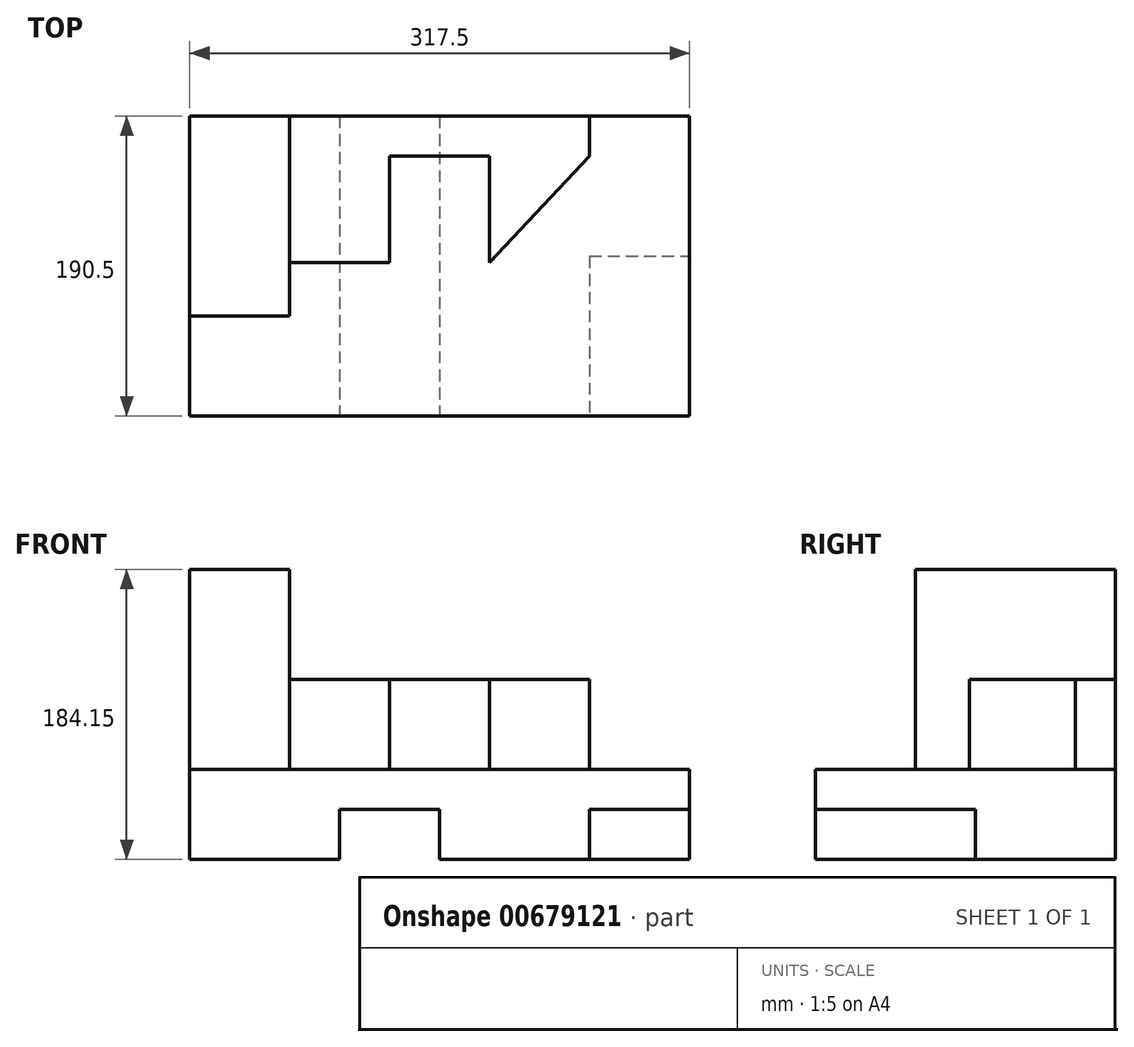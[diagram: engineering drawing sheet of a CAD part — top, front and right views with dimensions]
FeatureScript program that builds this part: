
annotation { "Feature Type Name" : "Feature", "Feature Type Description" : "" }
export const myFeature = defineFeature(function(context is Context, id is Id, definition is map)
    precondition{}
    {
        {
            var Q0;
            Q0=qCreatedBy(makeId("Front.planeOp"),FACE);
            var sketch = newSketch(context, id + "F0", { "sketchPlane" : qUnion([Q0])});
            skLineSegment(sketch, "E0.bottom", {"start": v(-158.75, 57.15) * mm, "end": v(158.75, 57.15) * mm});
            skLineSegment(sketch, "E0.top", {"start": v(-158.75, 0) * mm, "end": v(158.75, 0) * mm});
            skLineSegment(sketch, "E0.left", {"start": v(-158.75, 57.15) * mm, "end": v(-158.75, 0) * mm});
            skLineSegment(sketch, "E0.right", {"start": v(158.75, 57.15) * mm, "end": v(158.75, 0) * mm});
            skSolve(sketch);
        }
        {
            var Q0;
            Q0=makeQuery(id+"F0.imprint","IMPRINT",FACE,{"disambiguationData":[TD([[makeQuery(id+"F0.imprint","IMPRINT",EDGE,{"derivedFrom":sQuery(id+"F0.wireOp",EDGE,"E0.bottom")}),-1.0]])]});
            extrude(context, id + "F1", {"entities" : qUnion([Q0]), "oppositeDirection" : true, "depth" : 190.5 * mm, "offsetDistance" : 25.4 * mm});
        }
        {
            var Q0;
            Q0=makeQuery(id+"F1.opExtrude","CAP_FACE",FACE,{"disambiguationData":[OSD([sQuery(id+"F0.wireOp",EDGE,"E0.bottom"),sQuery(id+"F0.wireOp",EDGE,"E0.top"),sQuery(id+"F0.wireOp",EDGE,"E0.left"),sQuery(id+"F0.wireOp",EDGE,"E0.right")])],"isStart":true});
            var sketch = newSketch(context, id + "F2", { "sketchPlane" : qUnion([Q0])});
            skLineSegment(sketch, "E1", {"start": v(-63.5, 0) * mm, "end": v(-63.5, 31.75) * mm});
            skLineSegment(sketch, "E2", {"start": v(-63.5, 31.75) * mm, "end": v(0, 31.75) * mm});
            skLineSegment(sketch, "E3", {"start": v(0, 31.75) * mm, "end": v(0, 0) * mm});
            skLineSegment(sketch, "E4", {"start": v(0, 0) * mm, "end": v(-63.5, 0) * mm});
            skSolve(sketch);
        }
        {
            var Q0;
            Q0=makeQuery(id+"F2.imprint","IMPRINT",FACE,{"disambiguationData":[TD([[makeQuery(id+"F2.imprint","IMPRINT",EDGE,{"derivedFrom":sQuery(id+"F2.wireOp",EDGE,"E1")}),-1.0]])]});
            extrude(context, id + "F3", {"entities" : qUnion([Q0]), "operationType" : NewBodyOperationType.REMOVE, "endBound" : BoundingType.THROUGH_ALL, "oppositeDirection" : true, "depth" : 274.32 * mm, "offsetDistance" : 25.4 * mm});
        }
        {
            var Q0;
            Q0=makeQuery(id+"F0.imprint","IMPRINT",FACE,{"disambiguationData":[TD([[makeQuery(id+"F0.imprint","IMPRINT",EDGE,{"derivedFrom":sQuery(id+"F0.wireOp",EDGE,"E0.bottom")}),-1.0]])]});
            var sketch = newSketch(context, id + "F4", { "sketchPlane" : qUnion([Q0])});
            skLineSegment(sketch, "E5", {"start": v(158.75, 0) * mm, "end": v(158.75, 31.75) * mm});
            skLineSegment(sketch, "E6", {"start": v(158.75, 31.75) * mm, "end": v(95.25, 31.75) * mm});
            skLineSegment(sketch, "E7", {"start": v(95.25, 31.75) * mm, "end": v(95.25, 0) * mm});
            skLineSegment(sketch, "E8", {"start": v(95.25, 0) * mm, "end": v(158.75, 0) * mm});
            skSolve(sketch);
        }
        {
            var Q0;
            Q0=makeQuery(id+"F4.imprint","IMPRINT",FACE,{"disambiguationData":[TD([[makeQuery(id+"F4.imprint","IMPRINT",EDGE,{"derivedFrom":sQuery(id+"F4.wireOp",EDGE,"E5")}),-1.0]])]});
            extrude(context, id + "F5", {"entities" : qUnion([Q0]), "operationType" : NewBodyOperationType.REMOVE, "oppositeDirection" : true, "depth" : 101.6 * mm, "offsetDistance" : 25.4 * mm});
        }
        {
            var Q0;
            Q0=makeQuery(id+"F1.opExtrude","SWEPT_FACE",FACE,{"disambiguationData":[OSD([sQuery(id+"F0.wireOp",EDGE,"E0.bottom")])]});
            var sketch = newSketch(context, id + "F6", { "sketchPlane" : qUnion([Q0])});
            skLineSegment(sketch, "E9", {"start": v(-158.75, 190.5) * mm, "end": v(-158.75, 63.5) * mm});
            skLineSegment(sketch, "E10", {"start": v(-78.38, 190.5) * mm, "end": v(-158.75, 190.5) * mm});
            skLineSegment(sketch, "E11.0", {"start": v(-95.25, 190.5) * mm, "end": v(-95.25, 63.5) * mm});
            skLineSegment(sketch, "E12.0", {"start": v(-165.1, -6.35) * mm, "end": v(165.1, -6.35) * mm});
            skLineSegment(sketch, "E12.1", {"start": v(-165.1, 196.85) * mm, "end": v(-165.1, -6.35) * mm});
            skLineSegment(sketch, "E12.2", {"start": v(165.1, 196.85) * mm, "end": v(-165.1, 196.85) * mm});
            skLineSegment(sketch, "E12.3", {"start": v(165.1, -6.35) * mm, "end": v(165.1, 196.85) * mm});
            skLineSegment(sketch, "E13", {"start": v(-95.25, 63.5) * mm, "end": v(-158.75, 63.5) * mm});
            skSolve(sketch);
        }
        {
            var Q0;
            Q0=makeQuery(id+"F6.imprint","IMPRINT",FACE,{"disambiguationData":[TD([[makeQuery(id+"F6.imprint","IMPRINT",EDGE,{"derivedFrom":sQuery(id+"F6.wireOp",EDGE,"E9")}),1.0]])]});
            extrude(context, id + "F7", {"entities" : qUnion([Q0]), "operationType" : NewBodyOperationType.ADD, "depth" : 127 * mm, "offsetDistance" : 25.4 * mm});
        }
        {
            var Q0;
            Q0=makeQuery(id+"F1.opExtrude","SWEPT_FACE",FACE,{"disambiguationData":[OSD([sQuery(id+"F0.wireOp",EDGE,"E0.bottom")])]});
            var sketch = newSketch(context, id + "F8", { "sketchPlane" : qUnion([Q0])});
            skLineSegment(sketch, "E14", {"start": v(-95.25, 190.5) * mm, "end": v(-95.25, 97.55) * mm});
            skLineSegment(sketch, "E15", {"start": v(-95.25, 97.55) * mm, "end": v(-31.75, 97.55) * mm});
            skLineSegment(sketch, "E16", {"start": v(-31.75, 97.55) * mm, "end": v(-31.75, 165.1) * mm});
            skLineSegment(sketch, "E17", {"start": v(-31.75, 165.1) * mm, "end": v(31.75, 165.1) * mm});
            skLineSegment(sketch, "E18", {"start": v(31.75, 165.1) * mm, "end": v(31.75, 97.55) * mm});
            skLineSegment(sketch, "E19", {"start": v(31.75, 97.55) * mm, "end": v(95.25, 165.1) * mm});
            skLineSegment(sketch, "E20", {"start": v(95.25, 165.1) * mm, "end": v(95.25, 190.5) * mm});
            skSolve(sketch);
        }
        {
            var Q0;
            Q0 = qSketchRegion(id + "F8", true);
            var Q1;
            {var subQ0=sQuery(id+"F8.wireOp",EDGE,"E14");Q1=makeQuery(id+"F8.imprint","IMPRINT",FACE,{"disambiguationData":[TD([[makeQuery(id+"F8.imprint","IMPRINT",EDGE,{"derivedFrom":subQ0}),1.0]])]});}
            extrude(context, id + "F9", {"entities" : qUnion([Q0, Q1]), "operationType" : NewBodyOperationType.ADD, "depth" : 57.15 * mm, "offsetDistance" : 25.4 * mm});
        }
    });
